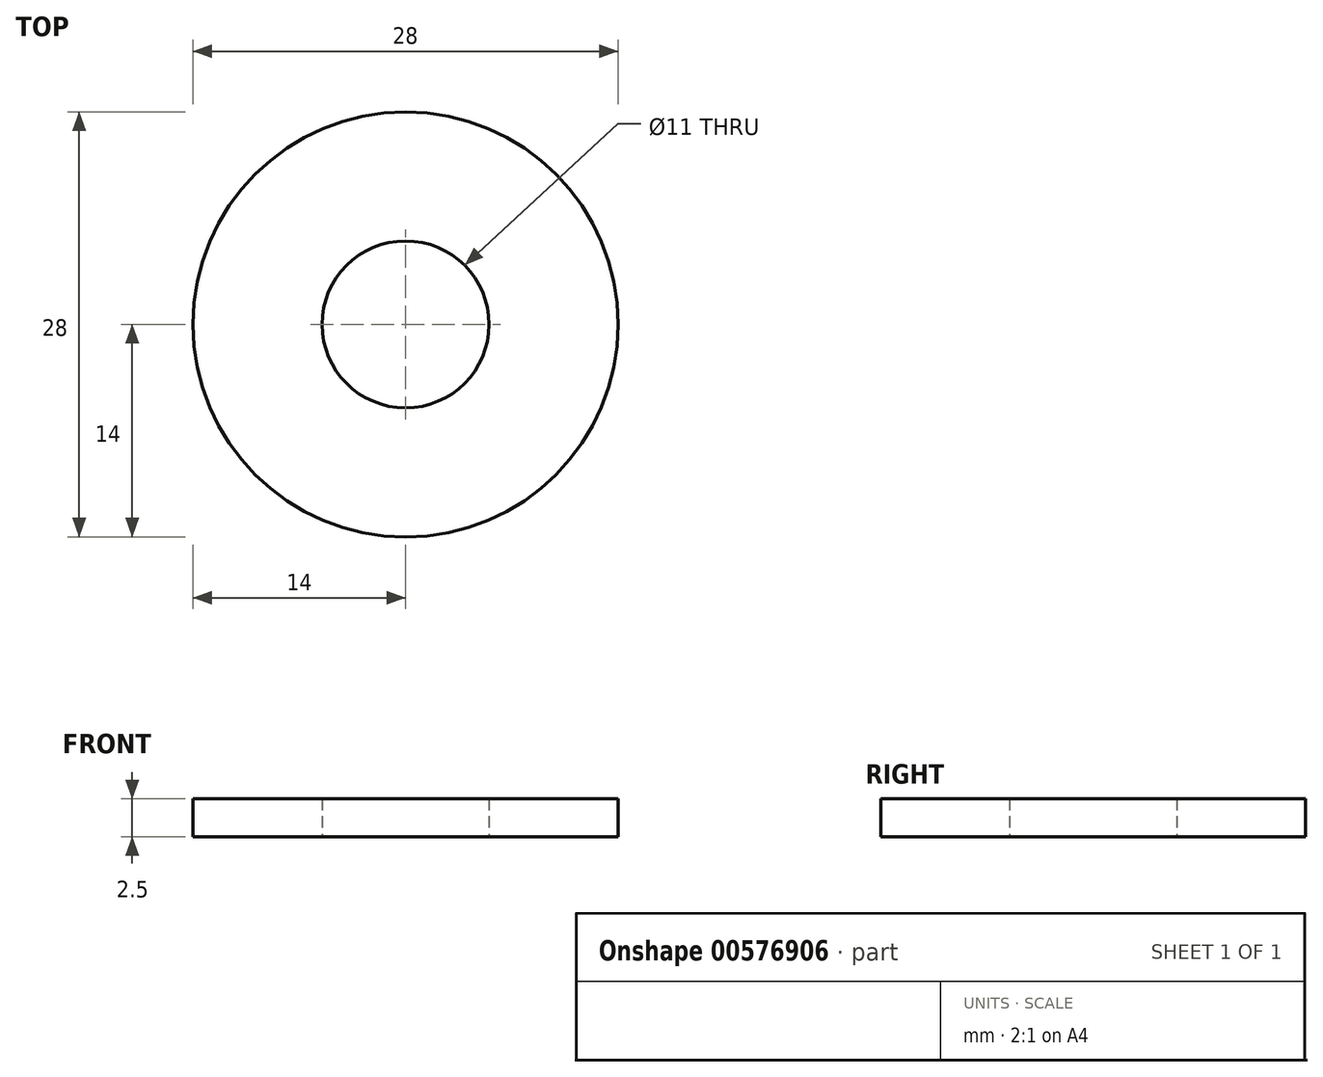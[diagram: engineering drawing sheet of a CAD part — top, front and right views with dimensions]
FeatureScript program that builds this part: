
annotation { "Feature Type Name" : "Feature", "Feature Type Description" : "" }
export const myFeature = defineFeature(function(context is Context, id is Id, definition is map)
    precondition{}
    {
        {
            var Q0;
            Q0=qCreatedBy(makeId("Top.planeOp"),FACE);
            var sketch = newSketch(context, id + "F0", { "sketchPlane" : qUnion([Q0])});
            skCircle(sketch, "E0", {"center": v(0, 0) * mm, "radius": 5.5 * mm});
            skCircle(sketch, "E1", {"center": v(0, 0) * mm, "radius": 14 * mm});
            skSolve(sketch);
        }
        {
            var Q0;
            Q0=qSketchRegion(id+"F0",true);
            extrude(context, id + "F1", {"entities" : qUnion([Q0]), "depth" : 2.5 * mm});
        }
    });
